# Revit family: tethys tavolino
name_source: partatom
category: Arredi
revit_build: Autodesk Revit 2017 (Build: 20161205_1400(x64)
units: mm (PartAtom-declared; Revit-internal decimal feet)

## family parameters
Basato su piano di lavoro = No
Condiviso = No
Numero OmniClass = 23.40.20.00
Punto di calcolo locali = No
Sempre verticale = Sì
Taglio con vuoti quando caricato = No
Titolo OmniClass = General Furniture and Specialties

## types (6) — shared parameters
Mat. Piano = Marmo
Mat. Struttura = Acciaio - Lucido
Mat. Vassoio = Acciaio - Lucido
Modello = Tethys tavolino
Produttore = Living Divani s.r.l.
URL = http://www.livingdivani.it

## per-type parameters (varying)
| type | Altezza | Codice Prodotto | Diametro | Visib. Piano legno | Visib. Piano pietra | Visib. Vassoio | posizione paletto | raggio | raggio interno | raggio interno meno 1 | raggio meno 1 |
| Diam 39 H51 Piano legno | 51 cm | TETV039 | 39 cm | Sì | No | No | 19 cm | 20 cm | 16 cm | 17 cm | 19 cm |
| Diam 39 H51 piano pietra | 51 cm | TETV039 | 39 cm | No | Sì | No | 19 cm | 20 cm | 16 cm | 17 cm | 19 cm |
| Diam 39 H51 Vassoio | 51 cm | TETV039 | 39 cm | No | No | Sì | 19 cm | 20 cm | 16 cm | 17 cm | 19 cm |
| Diam 49 H43 Piano legno | 43 cm | TETV049 | 49 cm | Sì | No | No | 24 cm | 25 cm | 21 cm | 22 cm | 24 cm |
| Diam 49 H43 piano pietra | 43 cm | TETV049 | 49 cm | No | Sì | No | 24 cm | 25 cm | 21 cm | 22 cm | 24 cm |
| Diam 49 H43 Vassoio | 43 cm | TETV049 | 49 cm | No | No | Sì | 24 cm | 25 cm | 21 cm | 22 cm | 24 cm |
